# Revit family: SDP-858I IP-видеокамера
name_source: partatom
category: Устройства связи
revit_build: Autodesk Revit 2017 (Build: 20170118_1100(x64)
units: mm (PartAtom-declared; Revit-internal decimal feet)

## family parameters
Всегда вертикально = Нет
На основе рабочей плоскости = Нет
Общий = Нет
При загрузке вырезать с полостями = Нет
Размер круглого соединителя = Использовать диаметр
Сохранять ориентацию аннотаций = Нет
Тип детали = Нормальный
Точка расчета площади = Нет

## types (1)
- SDP-858I IP-видеокамера
    ADSK_URL страницы изделия = https://stilsoft.ru
    ADSK_Единица измерения = шт.
    ADSK_Завод-изготовитель = ООО «Основа Безопасности»
    ADSK_Количество = 1
    ADSK_Марка = CТАЕ.426459.041-05
    ADSK_Масса = 1.2
    ADSK_Наименование = IP-видеокамера SDP-858I
    ADSK_Размер_Высота = 91 мм
    ADSK_Размер_Диаметр = 91 мм
    ADSK_Размер_Длина = 330 мм
    d_короба = 20 мм
    Дальность ИК подсветки, до, м = 70
    Диапазон рабочих температур, <unrecoverable-encoding: 5 bytes ef82b0d0a1> = от -45 до +50
    Максимальная потребляемая мощность, не более, Вт = 9
    Максимальное разрешение, пикс = 2592×1944
    Матрица = 1/2,8" Progressive Scan CMOS
    Мощность = 9
    Напряжение = 12
    Напряжение электропитания постоянного тока, В = 12, РоЕ (802.3af)
    Объектив, мм = 2.8 – 12 @ F1.4
    Поддерживаемые протоколы = IPv4/IPv6, TCP/UDP, HTTP, PPPoE, FTP, UPNP, DDNS, SMTP, SNMP, RTSP, ONVIF
    Режим «День/ночь» = Механический ИК-фильтр с автопереключением
    Сетевой интерфейс = 1 RJ45 10М/100М Ethernet порт
    Скорость передачи = 200Кб/сек – 12МБ/сек
    Угол обзора, ° = 86 – 26
    Управление = Веб-интерфейс, StilVL
    Формат сжатия = Н.265 / Н.264/MJPEG
    Чувствительность Цвет, Люкс = 0,01 / F1.2
    Чувствительность Ч/б, Люкс = 0,001 / F1.2
    Электронный затвор, сек. = 1/5-1/50000
